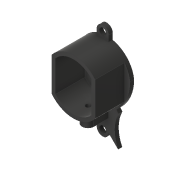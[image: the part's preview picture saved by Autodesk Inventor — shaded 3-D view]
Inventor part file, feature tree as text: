
AUTODESK INVENTOR PART (.ipt)
format: ipt  version: 2017 (Build 210142000, 142)  size: 214,016 bytes
history: native  units: in
note: dims shown in document units (in); Inventor stores cm internally (conversion verified against a paired STEP export)
features: extrude x6, sketch x6, reference x5, other x5, projected_geometry x2, plane x1
ambient origin geometry x8: Origin, YZ Plane, XZ Plane, XY Plane, X Axis, Y Axis, Z Axis, Center Point
bodies: Solid1 (feature_tree)
feature tree (25):
  extrude  "Extrusion1"  Depth=0.12in
  sketch  "Sketch2"  dims[d3=0.12in d4=0.1in]
  plane  "Work Plane1"
  extrude  "Extrusion3"  Depth=0.1in
  extrude  "Extrusion4"  Depth=0.1in
  extrude  "Extrusion5"  Depth=0.5in TaperAngle=0.0deg
  extrude  "Extrusion6"  Depth=0.375in TaperAngle=0.0deg
  extrude  "Extrusion7"  Depth=0.5in TaperAngle=0.0deg
  sketch  "Sketch1"  dims[d0=0.0669in d1=0.0in d2=0.12in]
  reference  "Reference1"
  sketch  "Sketch3"  dims[d5=0.1in d8=0.01in]
  reference  "Reference2"
  reference  "Reference3"
  reference  "Reference4"
  reference  "Reference5"
  projected_geometry  "Projected Loop1"
  sketch  "Sketch4"  dims[d9=0.5in d10=0.0in d11=0.5in d12=0.0in]
  sketch  "Sketch5"  dims[d13=0.375in d14=0.0in d15=0.375in d16=0.0in]
  projected_geometry  "Projected Loop2"
  sketch  "Sketch6"  dims[d17=0.08in d18=0.5in d19=0.0in]
  parser-record x1  (decoder bookkeeping rows leaked as tree rows — omitted from the tree; the rows remain in map.json)
  other  "Assembly with Fan.iam"
  other  "Bottom Assembly:1"
  other  "Bottom:1"
  other  "Size 130 Motor:1"
note: 1 file-system path scrubbed to <path> (originals preserved in map.json)
